# Revit family: EU_EHS_Mono_Tank_Hyd_Unit_200L,260L_Ver._1.0
name_source: partatom
category: Mechanical Equipment
revit_build: Autodesk Revit 2016 (Build: 20150220_1215(x64)
units: mm (PartAtom-declared; Revit-internal decimal feet)

## family parameters
Always vertical = Yes
Cut with Voids When Loaded = No
OmniClass Number = 23.75.00.00
OmniClass Title = Climate Control (HVAC)
Part Type = Normal
Room Calculation Point = No
Round Connector Dimension = Use Diameter
Shared = No
Work Plane-Based = No

## types (10) — shared parameters
Description = -
Manufacturer = SAMSUNG
Motor Ouput = 0.00 W
URL = www.samsung.com

## per-type parameters (varying)
| type | Model |
| 5.00 kW, 220-240V, HEAT PUMP, Mono | AE050RXYDEG/EU |
| 8.00 kW, 220-240V, HEAT PUMP, Mono | AE080RXYDEG/EU |
| 12.00 kW, 200L, 220-240V, HEAT PUMP, Mono | AE120RXYDEG/EU |
| 16.00 kW, 200L, 220-240V, HEAT PUMP, Mono | AE160RXYDEG/EU |
| 8.00 kW, 260L, 220-240V, HEAT PUMP, Mono | AE080RXYDEG/EU |
| 12.00 kW, 260L, 220-240V, HEAT PUMP, Mono | AE120RXYDEG/EU |
| 16.00 kW, 260L, 220-240V, HEAT PUMP, Mono | AE160RXYDEG/EU |
| 8.00 kW, 260L, 380-415V, HEAT PUMP, Mono | AE090RXYDGG/EU |
| 12.00 kW, 260L, 380-415V, HEAT PUMP, Mono | AE120RXYDGG/EU |
| 16.00 kW, 260L, 380-415V, HEAT PUMP, Mono | AE160RXYDGG/EU |

## geometry (parser evidence)
native form markers: Sweep x1
no freeform markers — native parametric forms only
